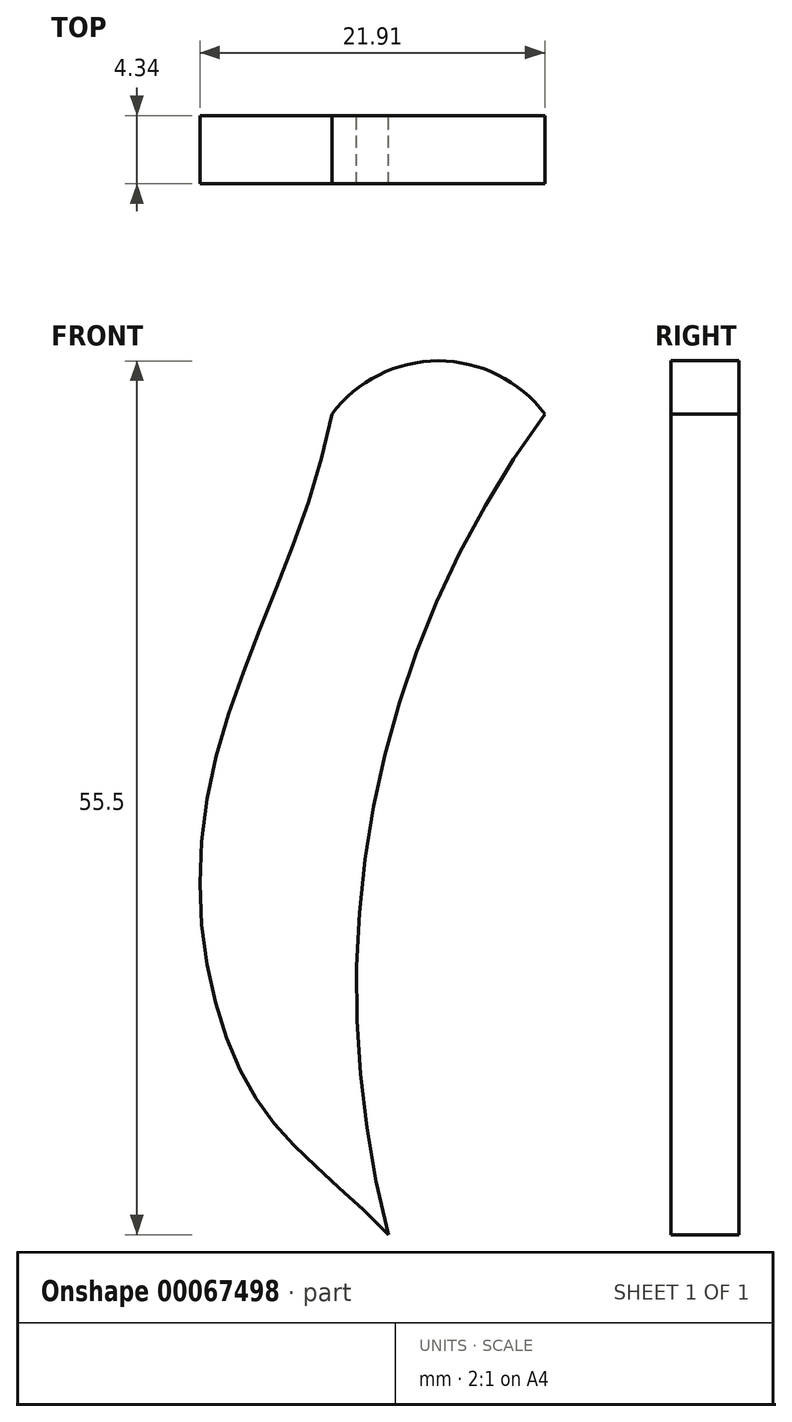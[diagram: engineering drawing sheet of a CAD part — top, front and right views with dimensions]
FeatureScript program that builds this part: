
annotation { "Feature Type Name" : "Feature", "Feature Type Description" : "" }
export const myFeature = defineFeature(function(context is Context, id is Id, definition is map)
    precondition{}
    {
        {
            var Q0;
            Q0=qCreatedBy(makeId("Front.planeOp"),FACE);
            var sketch = newSketch(context, id + "F0", { "sketchPlane" : qUnion([Q0])});
            skArc(sketch, "E0", {"start": v(-9.48, -7.8) * mm, "mid": v(-20.36, -32.73) * mm, "end": v(-19.4, -59.92) * mm});
            skFitSpline(sketch, "E1", {"points": [v(-19.4, -59.92) * mm, v(-28.17, -50.68) * mm, v(-30.94, -32.21) * mm, v(-23, -7.8) * mm], "startDerivative": vector(-37.8, 38.56) * mm, "endDerivative": vector(12.51, 65.02) * mm});
            skArc(sketch, "E2", {"start": v(-9.48, -7.8) * mm, "mid": v(-16.24, -4.42) * mm, "end": v(-23, -7.8) * mm});
            skSolve(sketch);
        }
        {
            var Q0;
            Q0 = qSketchRegion(id + "F0", true);
            extrude(context, id + "F1", {"entities" : qUnion([Q0]), "depth" : 4.34 * mm});
        }
    });
